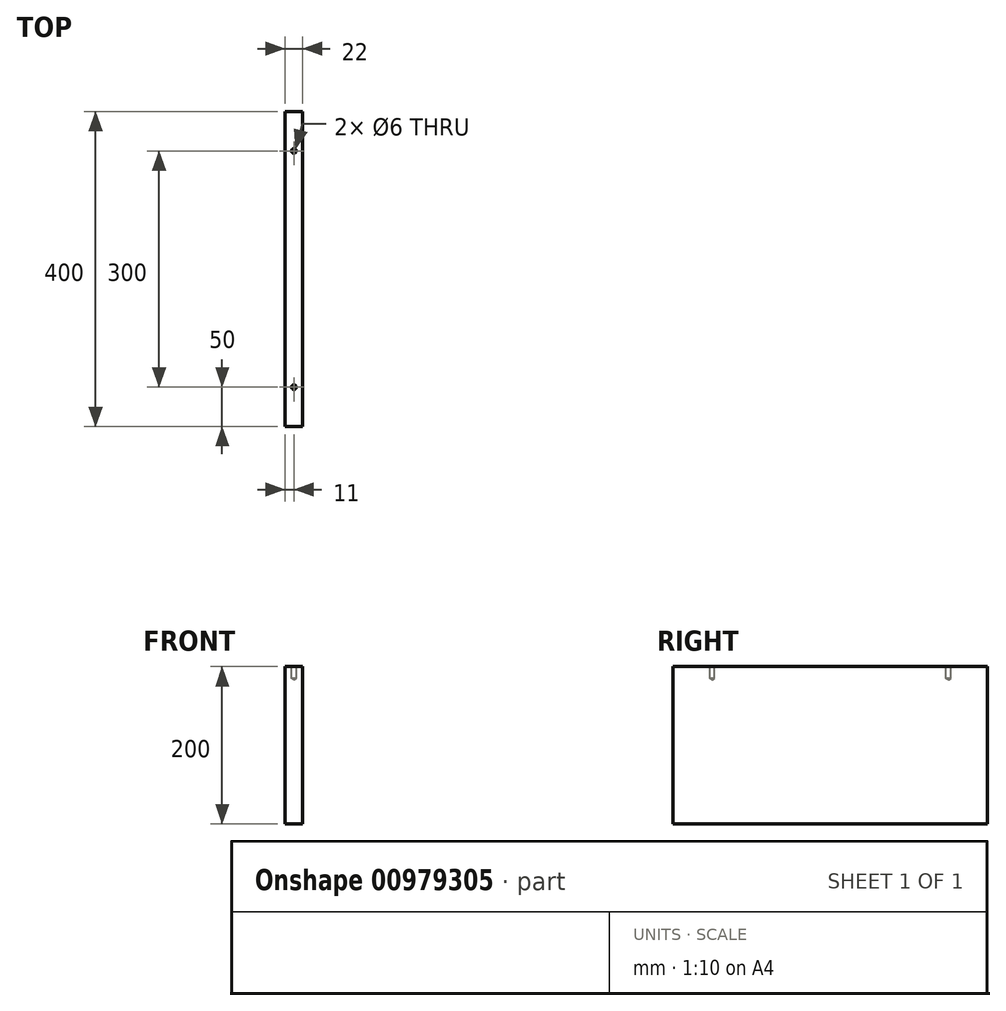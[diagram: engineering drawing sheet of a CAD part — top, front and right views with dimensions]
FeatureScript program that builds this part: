
annotation { "Feature Type Name" : "Feature", "Feature Type Description" : "" }
export const myFeature = defineFeature(function(context is Context, id is Id, definition is map)
    precondition{}
    {
        {
            var Q0;
            Q0=qCreatedBy(makeId("Right.planeOp"),FACE);
            var sketch = newSketch(context, id + "F0", { "sketchPlane" : qUnion([Q0])});
            skLineSegment(sketch, "E0.bottom", {"start": v(0, 0) * mm, "end": v(400, 0) * mm});
            skLineSegment(sketch, "E0.top", {"start": v(0, 200) * mm, "end": v(400, 200) * mm});
            skLineSegment(sketch, "E0.left", {"start": v(0, 0) * mm, "end": v(0, 200) * mm});
            skLineSegment(sketch, "E0.right", {"start": v(400, 0) * mm, "end": v(400, 200) * mm});
            skSolve(sketch);
        }
        {
            var Q0;
            Q0=makeQuery(id+"F0.imprint","IMPRINT",FACE,{"disambiguationData":[TD([[makeQuery(id+"F0.imprint","IMPRINT",EDGE,{"derivedFrom":sQuery(id+"F0.wireOp",EDGE,"E0.bottom")}),1.0]])]});
            extrude(context, id + "F1", {"entities" : qUnion([Q0]), "depth" : 22 * mm, "offsetDistance" : 25 * mm});
        }
        {
            var Q0;
            Q0=makeQuery(id+"F1.opExtrude","SWEPT_FACE",FACE,{"disambiguationData":[OSD([sQuery(id+"F0.wireOp",EDGE,"E0.top")])]});
            var sketch = newSketch(context, id + "F2", { "sketchPlane" : qUnion([Q0])});
            skPoint(sketch, "E1", {"position": v(11, 50) * mm});
            skPoint(sketch, "E2", {"position": v(11, 350) * mm});
            skLineSegment(sketch, "E3", {"start": v(11, 0) * mm, "end": v(11, 400) * mm, "construction": true});
            skSolve(sketch);
        }
        {
            var Q0;
            Q0=sQuery(id+"F2.wireOp",VERTEX,"E2");
            var Q1;
            Q1=sQuery(id+"F2.wireOp",VERTEX,"E1");
            var Q2;
            Q2=makeQuery(id+"F1.opExtrude","SWEPT_BODY",BODY,{"disambiguationData":[OSD([sQuery(id+"F0.wireOp",EDGE,"E0.bottom"),sQuery(id+"F0.wireOp",EDGE,"E0.top"),sQuery(id+"F0.wireOp",EDGE,"E0.left"),sQuery(id+"F0.wireOp",EDGE,"E0.right")])]});
            hole(context, id + "F3", {"style" : HoleStyle.SIMPLE, "endStyle" : HoleEndStyle.BLIND, "standardTappedOrClearance" : lookupTablePath({ "standard" : "ISO", "size" : "6", "type" : "Drilled" }), "standardBlindInLast" : lookupTablePath({ "standard" : "ISO", "size" : "6", "type" : "Drilled" }), "holeDiameter" : 6 * mm, "majorDiameter" : 8 * mm, "holeDepth" : 15 * mm, "isTappedThrough" : true, "tappedDepth" : 12 * mm, "tapClearance" : 3, "startFromSketch" : true, "locations" : qUnion([Q0, Q1]), "scope" : qUnion([Q2])});
        }
    });
